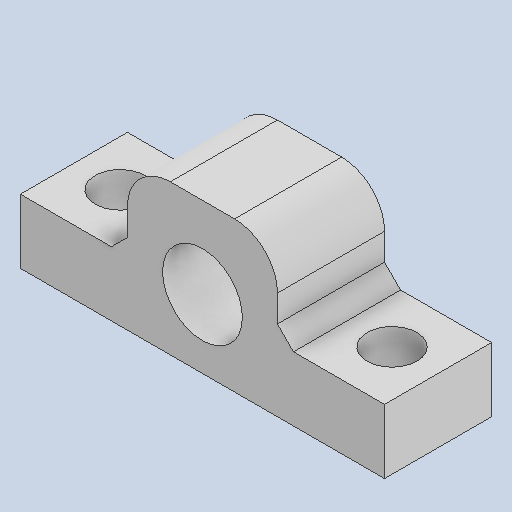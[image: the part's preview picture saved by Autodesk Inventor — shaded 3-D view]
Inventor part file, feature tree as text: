
AUTODESK INVENTOR PART (.ipt)
format: ipt  version: 2022 (Build 260153000, 153)  size: 154,112 bytes
history: native  units: mm
features: extrude x4, sketch x4, fillet x1, chamfer x1
ambient origin geometry x8: Origin, YZ Plane, XZ Plane, XY Plane, X Axis, Y Axis, Z Axis, Center Point
bodies: Solid1 (feature_tree)
feature tree (10):
  extrude  "Extrusion1"  Depth=10.0mm
  extrude  "Extrusion2"  Depth=6.0mm
  extrude  "Extrusion3"  Depth=4.65mm
  extrude  "Extrusion4"  Depth=10.0mm
  fillet  "Fillet2"  Radius=4.3mm
  chamfer  "Chamfer1"  [1 undecoded]
  sketch  "Sketch1"  dims[d0=34.0mm d1=10.0mm]
  sketch  "Sketch3"  dims[d2=6.0mm d3=0.0mm d4=4.65mm]
  sketch  "Sketch4"  dims[d5=5.0mm d6=4.65mm]
  sketch  "Sketch6"  dims[d7=5.0mm d9=4.3mm d10=4.3mm d11=0.0mm d12=0.0mm d16=8.0mm d17=0.0mm d26=7.45mm d29=0.0mm d30=0.0mm d31=4.0mm d34=14.0mm d35=10.0mm d36=7.62mm d37=7.0mm d39=1.5mm d40=2.0mm d41=45.0deg]
note: 1 required parameter value undecoded (feature->parameter linkage not recoverable at this tier; creation-order binding heuristic only, values carry confidence <= 0.55)
